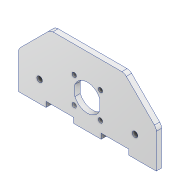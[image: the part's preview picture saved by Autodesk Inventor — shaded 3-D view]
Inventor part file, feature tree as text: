
AUTODESK INVENTOR PART (.ipt)
format: ipt  version: 2020 (Build 240168000, 168)  size: 212,992 bytes
history: native  units: mm
features: other x3, sketch x3, extrude x2
ambient origin geometry x8: Origin, YZ Plane, XZ Plane, XY Plane, X Axis, Y Axis, Z Axis, Center Point
bodies: Body1 (feature_tree)
feature tree (8):
  other  "솔리드1"
  other  "모서리 라운드2"
  extrude  "돌출1"  Depth=40.0mm TaperAngle=360.0deg
  extrude  "돌출2"  Depth=20.0mm
  sketch  "스케치1"
  sketch  "스케치2"
  sketch  "스케치3"
  other  "정의1"
